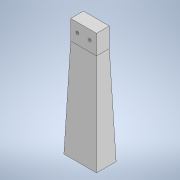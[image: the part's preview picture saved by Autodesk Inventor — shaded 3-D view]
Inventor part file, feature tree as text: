
AUTODESK INVENTOR PART (.ipt)
format: ipt  version: 2021 (Build 250183000, 183)  size: 128,512 bytes
history: native  units: mm
features: sketch x4, extrude x2, hole x2, projected_geometry x2, other x1
ambient origin geometry x8: Origin, YZ Plane, XZ Plane, XY Plane, X Axis, Y Axis, Z Axis, Center Point
bodies: Body1 (feature_tree)
feature tree (11):
  other  "實體1"
  extrude  "擠出1"  Depth=25.0mm
  extrude  "擠出2"  Depth=15.0mm
  hole  "孔1"  [1 undecoded]
  hole  "孔2"  [1 undecoded]
  sketch  "草圖1"
  sketch  "草圖2"
  projected_geometry  "投影迴路1"
  sketch  "草圖3"
  projected_geometry  "投影迴路2"
  sketch  "草圖4"
note: 2 required parameter values undecoded (feature->parameter linkage not recoverable at this tier; creation-order binding heuristic only, values carry confidence <= 0.55)
